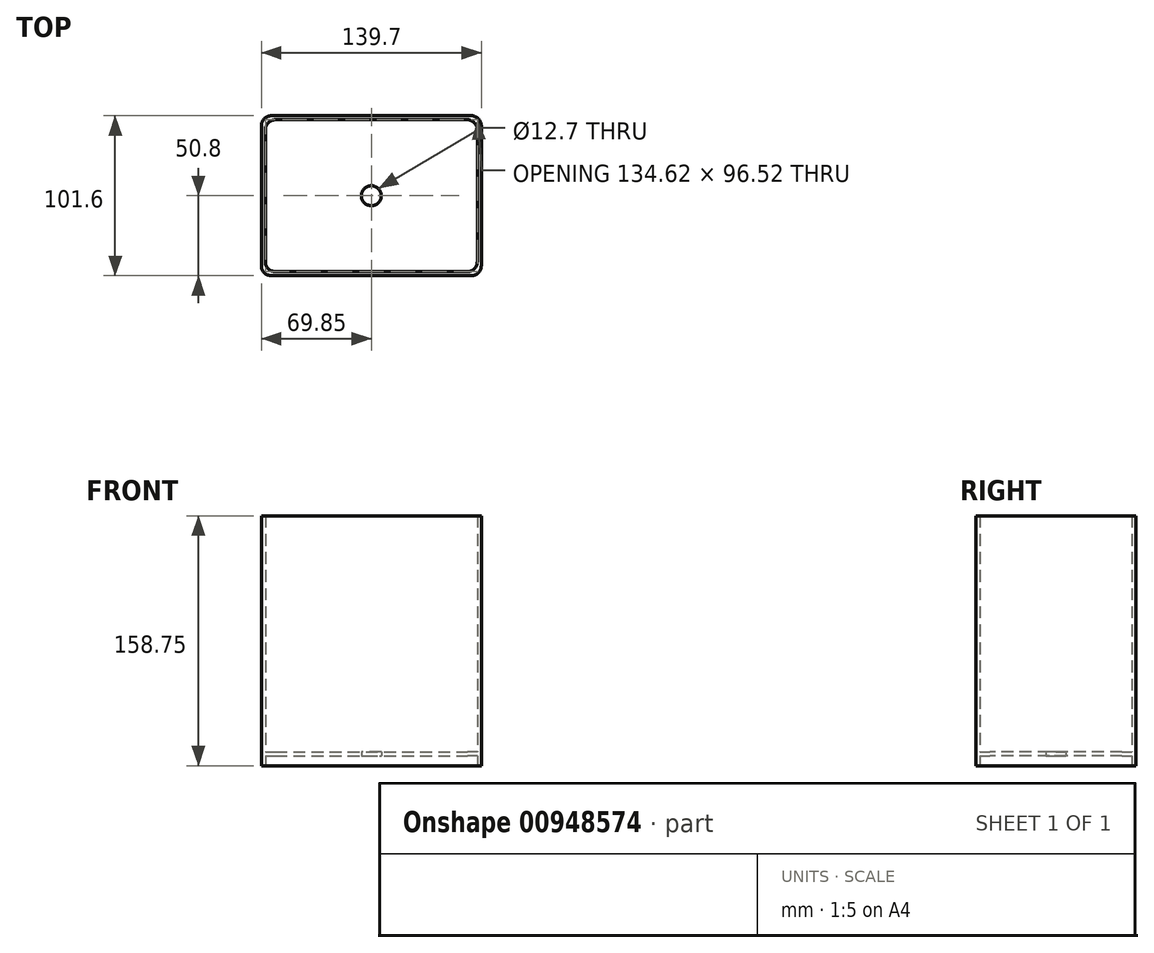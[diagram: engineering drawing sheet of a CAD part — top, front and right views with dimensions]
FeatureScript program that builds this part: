
annotation { "Feature Type Name" : "Feature", "Feature Type Description" : "" }
export const myFeature = defineFeature(function(context is Context, id is Id, definition is map)
    precondition{}
    {
        {
            var Q0;
            Q0=qCreatedBy(makeId("Top.planeOp"),FACE);
            var sketch = newSketch(context, id + "F0", { "sketchPlane" : qUnion([Q0])});
            skLineSegment(sketch, "E0.bottom", {"start": v(-63.5, 50.8) * mm, "end": v(63.5, 50.8) * mm});
            skLineSegment(sketch, "E0.top", {"start": v(-63.5, -50.8) * mm, "end": v(63.5, -50.8) * mm});
            skLineSegment(sketch, "E0.left", {"start": v(-69.85, 44.45) * mm, "end": v(-69.85, -44.45) * mm});
            skLineSegment(sketch, "E0.right", {"start": v(69.85, 44.45) * mm, "end": v(69.85, -44.45) * mm});
            skPoint(sketch, "E0.middle", {"position": v(0, 0) * mm});
            skLineSegment(sketch, "E1.bottom", {"start": v(-60.96, 48.26) * mm, "end": v(60.96, 48.26) * mm});
            skLineSegment(sketch, "E1.top", {"start": v(-60.96, -48.26) * mm, "end": v(60.96, -48.26) * mm});
            skLineSegment(sketch, "E1.left", {"start": v(-67.3, 41.9) * mm, "end": v(-67.3, -41.91) * mm});
            skLineSegment(sketch, "E1.right", {"start": v(67.3, 41.9) * mm, "end": v(67.3, -41.9) * mm});
            skPoint(sketch, "E2.visualSharp", {"position": v(-69.85, 50.8) * mm});
            skArc(sketch, "E2.filletArc", {"start": v(-63.5, 50.8) * mm, "mid": v(-68, 48.94) * mm, "end": v(-69.85, 44.45) * mm});
            skPoint(sketch, "E3.visualSharp", {"position": v(69.85, 50.8) * mm});
            skArc(sketch, "E3.filletArc", {"start": v(69.85, 44.45) * mm, "mid": v(68, 48.94) * mm, "end": v(63.5, 50.8) * mm});
            skPoint(sketch, "E4.visualSharp", {"position": v(67.3, 48.26) * mm});
            skArc(sketch, "E4.filletArc", {"start": v(67.3, 41.9) * mm, "mid": v(65.45, 46.4) * mm, "end": v(60.96, 48.26) * mm});
            skPoint(sketch, "E5.visualSharp", {"position": v(64.77, 45.72) * mm});
            skPoint(sketch, "E6.visualSharp", {"position": v(-64.77, 45.72) * mm});
            skPoint(sketch, "E7.visualSharp", {"position": v(-67.3, 48.26) * mm});
            skArc(sketch, "E7.filletArc", {"start": v(-60.96, 48.26) * mm, "mid": v(-65.45, 46.4) * mm, "end": v(-67.3, 41.9) * mm});
            skPoint(sketch, "E8.visualSharp", {"position": v(64.77, -45.72) * mm});
            skPoint(sketch, "E9.visualSharp", {"position": v(67.3, -48.26) * mm});
            skArc(sketch, "E9.filletArc", {"start": v(60.96, -48.26) * mm, "mid": v(65.45, -46.4) * mm, "end": v(67.3, -41.9) * mm});
            skPoint(sketch, "E10.visualSharp", {"position": v(69.85, -50.8) * mm});
            skArc(sketch, "E10.filletArc", {"start": v(63.5, -50.8) * mm, "mid": v(68, -48.94) * mm, "end": v(69.85, -44.45) * mm});
            skPoint(sketch, "E11.visualSharp", {"position": v(-69.85, -50.8) * mm});
            skArc(sketch, "E11.filletArc", {"start": v(-69.85, -44.45) * mm, "mid": v(-68, -48.94) * mm, "end": v(-63.5, -50.8) * mm});
            skPoint(sketch, "E12.visualSharp", {"position": v(-67.3, -48.26) * mm});
            skArc(sketch, "E12.filletArc", {"start": v(-67.3, -41.91) * mm, "mid": v(-65.45, -46.4) * mm, "end": v(-60.96, -48.26) * mm});
            skPoint(sketch, "E13.visualSharp", {"position": v(-64.77, -45.72) * mm});
            skSolve(sketch);
        }
        {
            var Q0;
            Q0=makeQuery(id+"F0.imprint","IMPRINT",FACE,{"disambiguationData":[TD([[makeQuery(id+"F0.imprint","IMPRINT",EDGE,{"derivedFrom":sQuery(id+"F0.wireOp",EDGE,"E0.bottom")}),-1.0]])]});
            extrude(context, id + "F1", {"entities" : qUnion([Q0]), "depth" : 152.4 * mm, "offsetDistance" : 25.4 * mm});
        }
        {
            var Q0;
            Q0=makeQuery(id+"F0.imprint","IMPRINT",FACE,{"disambiguationData":[TD([[makeQuery(id+"F0.imprint","IMPRINT",EDGE,{"derivedFrom":sQuery(id+"F0.wireOp",EDGE,"E0.bottom")}),-1.0]])]});
            extrude(context, id + "F2", {"entities" : qUnion([Q0]), "operationType" : NewBodyOperationType.ADD, "oppositeDirection" : true, "depth" : 6.35 * mm, "offsetDistance" : 25.4 * mm});
        }
        {
            var Q0;
            Q0=makeQuery(id+"F0.imprint","IMPRINT",FACE,{"disambiguationData":[TD([[makeQuery(id+"F0.imprint","IMPRINT",EDGE,{"derivedFrom":sQuery(id+"F0.wireOp",EDGE,"E1.bottom")}),-1.0]])]});
            extrude(context, id + "F3", {"entities" : qUnion([Q0]), "operationType" : NewBodyOperationType.ADD, "depth" : 2.54 * mm, "offsetDistance" : 25.4 * mm});
        }
        {
            var Q0;
            Q0=sQuery(id+"F0.wireOp",VERTEX,"E0.middle");
            var Q1;
            Q1=makeQuery(id+"F1.opExtrude","SWEPT_BODY",BODY,{"disambiguationData":[OSD([sQuery(id+"F0.wireOp",EDGE,"E0.bottom"),sQuery(id+"F0.wireOp",EDGE,"E0.top"),sQuery(id+"F0.wireOp",EDGE,"E0.left"),sQuery(id+"F0.wireOp",EDGE,"E0.right"),sQuery(id+"F0.wireOp",EDGE,"E1.bottom"),sQuery(id+"F0.wireOp",EDGE,"E1.top"),sQuery(id+"F0.wireOp",EDGE,"E1.left"),sQuery(id+"F0.wireOp",EDGE,"E1.right"),sQuery(id+"F0.wireOp",EDGE,"E2.filletArc"),sQuery(id+"F0.wireOp",EDGE,"E3.filletArc"),sQuery(id+"F0.wireOp",EDGE,"E4.filletArc"),sQuery(id+"F0.wireOp",EDGE,"E7.filletArc"),sQuery(id+"F0.wireOp",EDGE,"E9.filletArc"),sQuery(id+"F0.wireOp",EDGE,"E10.filletArc"),sQuery(id+"F0.wireOp",EDGE,"E11.filletArc"),sQuery(id+"F0.wireOp",EDGE,"E12.filletArc")])]});
            hole(context, id + "F4", {"style" : HoleStyle.SIMPLE, "endStyle" : HoleEndStyle.THROUGH, "oppositeDirection" : true, "holeDiameter" : 12.7 * mm, "majorDiameter" : 6.35 * mm, "isTappedThrough" : true, "tappedDepth" : 12.7 * mm, "tapClearance" : 3, "locations" : qUnion([Q0]), "scope" : qUnion([Q1])});
        }
    });
